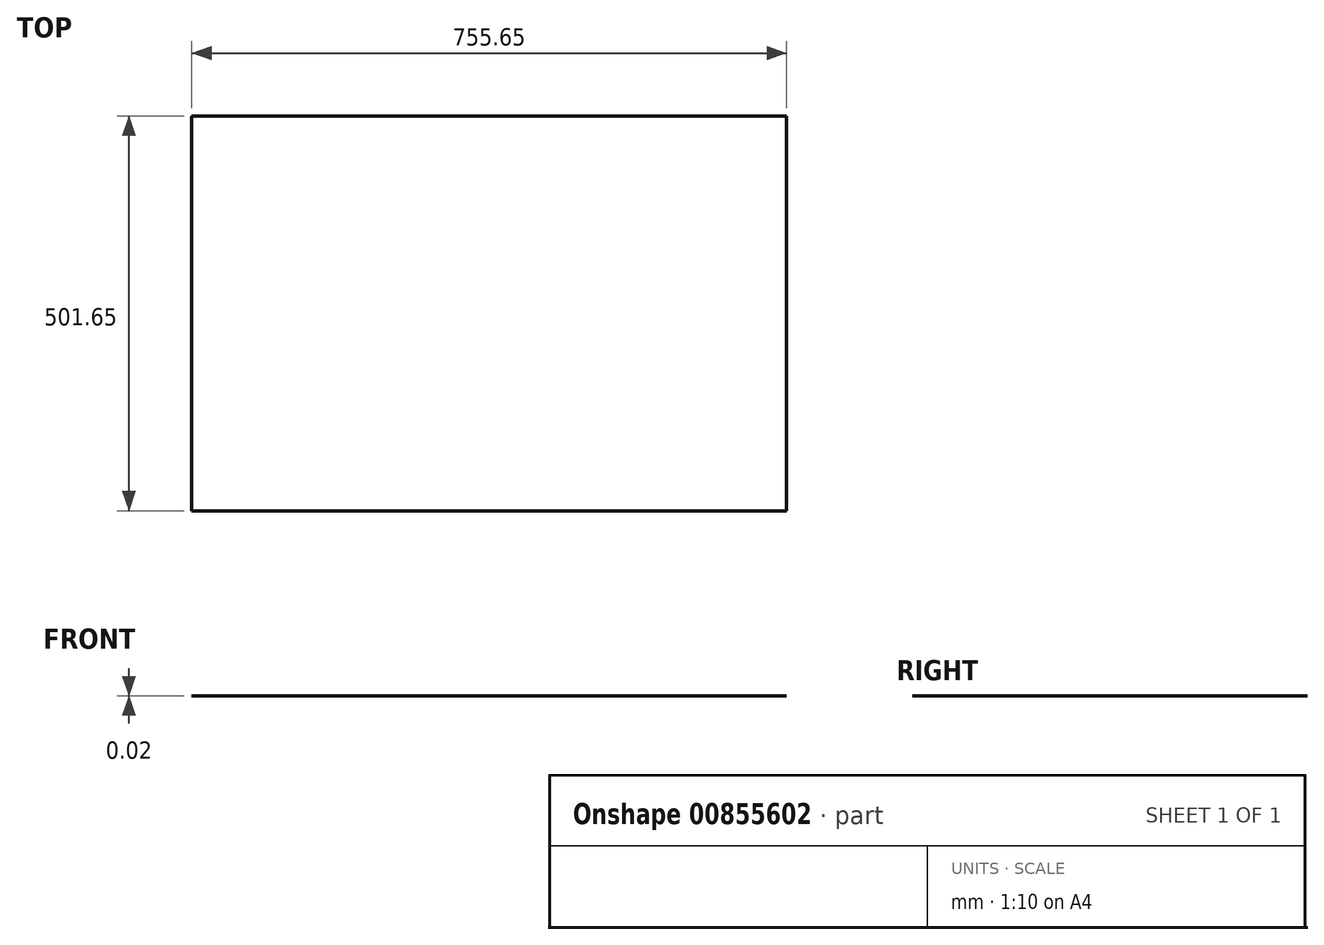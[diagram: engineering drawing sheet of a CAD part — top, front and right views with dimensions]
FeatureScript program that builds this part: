
annotation { "Feature Type Name" : "Feature", "Feature Type Description" : "" }
export const myFeature = defineFeature(function(context is Context, id is Id, definition is map)
    precondition{}
    {
        {
            var Q0;
            Q0=qCreatedBy(makeId("Top.planeOp"),FACE);
            var sketch = newSketch(context, id + "F0", { "sketchPlane" : qUnion([Q0])});
            skLineSegment(sketch, "E0.bottom", {"start": v(0, 0) * mm, "end": v(755.65, 0) * mm});
            skLineSegment(sketch, "E0.top", {"start": v(0, 501.65) * mm, "end": v(755.65, 501.65) * mm});
            skLineSegment(sketch, "E0.left", {"start": v(0, 0) * mm, "end": v(0, 501.65) * mm});
            skLineSegment(sketch, "E0.right", {"start": v(755.65, 0) * mm, "end": v(755.65, 501.65) * mm});
            skSolve(sketch);
        }
        {
            var Q0;
            Q0 = qSketchRegion(id + "F0", true);
            extrude(context, id + "F1", {"entities" : qUnion([Q0]), "depth" : 5 / 203.2 * mm, "offsetDistance" : 25.4 * mm});
        }
    });
